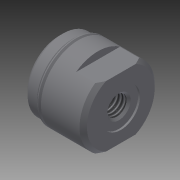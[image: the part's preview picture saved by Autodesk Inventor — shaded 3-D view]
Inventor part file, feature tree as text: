
AUTODESK INVENTOR PART (.ipt)
format: ipt  version: 2014 (Build 180170000, 170)  size: 200,704 bytes
history: native  units: in
note: dims shown in document units (in); Inventor stores cm internally (conversion verified against a paired STEP export)
features: other x63, sketch x5, revolve x3, extrude x1, hole x1, thread x1
ambient origin geometry x8: Origin, YZ Plane, XZ Plane, XY Plane, X Axis, Y Axis, Z Axis, Center Point
bodies: Solid1 (feature_tree)
feature tree (74):
  revolve  "Revolution1"  [1 undecoded]
  extrude  "Extrusion1"  TaperAngle=360.0deg  [1 undecoded]
  hole  "Hole1"  [1 undecoded]
  revolve  "Revolution2"  [1 undecoded]
  thread  "Thread1"  [1 undecoded]
  revolve  "Revolution3"  [1 undecoded]
  other  "aa2_XY"
  other  "aa2_YZ"
  other  "aa2_ZX"
  other  "aa2_X"
  other  "aa2_Y"
  other  "aa2_Z"
  other  "aa2_Center"
  other  "m1_XY"
  other  "m1_YZ"
  other  "m1_ZX"
  other  "m1_X"
  other  "m1_Y"
  other  "m1_Z"
  other  "m1_Center"
  other  "m2_XY"
  other  "m2_YZ"
  other  "m2_ZX"
  other  "m2_X"
  other  "m2_Y"
  other  "m2_Z"
  other  "m2_Center"
  other  "n1_XY"
  other  "n1_YZ"
  other  "n1_ZX"
  other  "n1_X"
  other  "n1_Y"
  other  "n1_Z"
  other  "n1_Center"
  other  "n2_XY"
  other  "n2_YZ"
  other  "n2_ZX"
  other  "n2_X"
  other  "n2_Y"
  other  "n2_Z"
  other  "n2_Center"
  other  "rear_head_XY"
  other  "rear_head_YZ"
  other  "rear_head_ZX"
  other  "rear_head_X"
  other  "rear_head_Y"
  other  "rear_head_Z"
  other  "rear_head_Center"
  other  "to_bushing_XY"
  other  "to_bushing_YZ"
  other  "to_bushing_ZX"
  other  "to_bushing_X"
  other  "to_bushing_Y"
  other  "to_bushing_Z"
  other  "to_bushing_Center"
  other  "to_mounting_bracket_xp_XY"
  other  "to_mounting_bracket_xp_YZ"
  other  "to_mounting_bracket_xp_ZX"
  other  "to_mounting_bracket_xp_X"
  other  "to_mounting_bracket_xp_Y"
  other  "to_mounting_bracket_xp_Z"
  other  "to_mounting_bracket_xp_Center"
  other  "to_pivot_bracket_XY"
  other  "to_pivot_bracket_YZ"
  other  "to_pivot_bracket_ZX"
  other  "to_pivot_bracket_X"
  other  "to_pivot_bracket_Y"
  other  "to_pivot_bracket_Z"
  other  "to_pivot_bracket_Center"
  sketch  "Sketch_1"  dims[d0=360.0deg d1=0.185in d2=0.0in]
  sketch  "Sketch_2"  dims[d3=0.375in d4=0.75in d5=0.395in d6=0.25in d7=90.0deg d8=0.188in d9=0.0in d10=360.0deg]
  sketch  "Sketch3"  dims[d11=0.185in d12=0.112in d13=360.0deg]
  sketch  "Sketch_5"
  sketch  "Sketch_9"
note: 6 required parameter values undecoded (feature->parameter linkage not recoverable at this tier; creation-order binding heuristic only, values carry confidence <= 0.55)